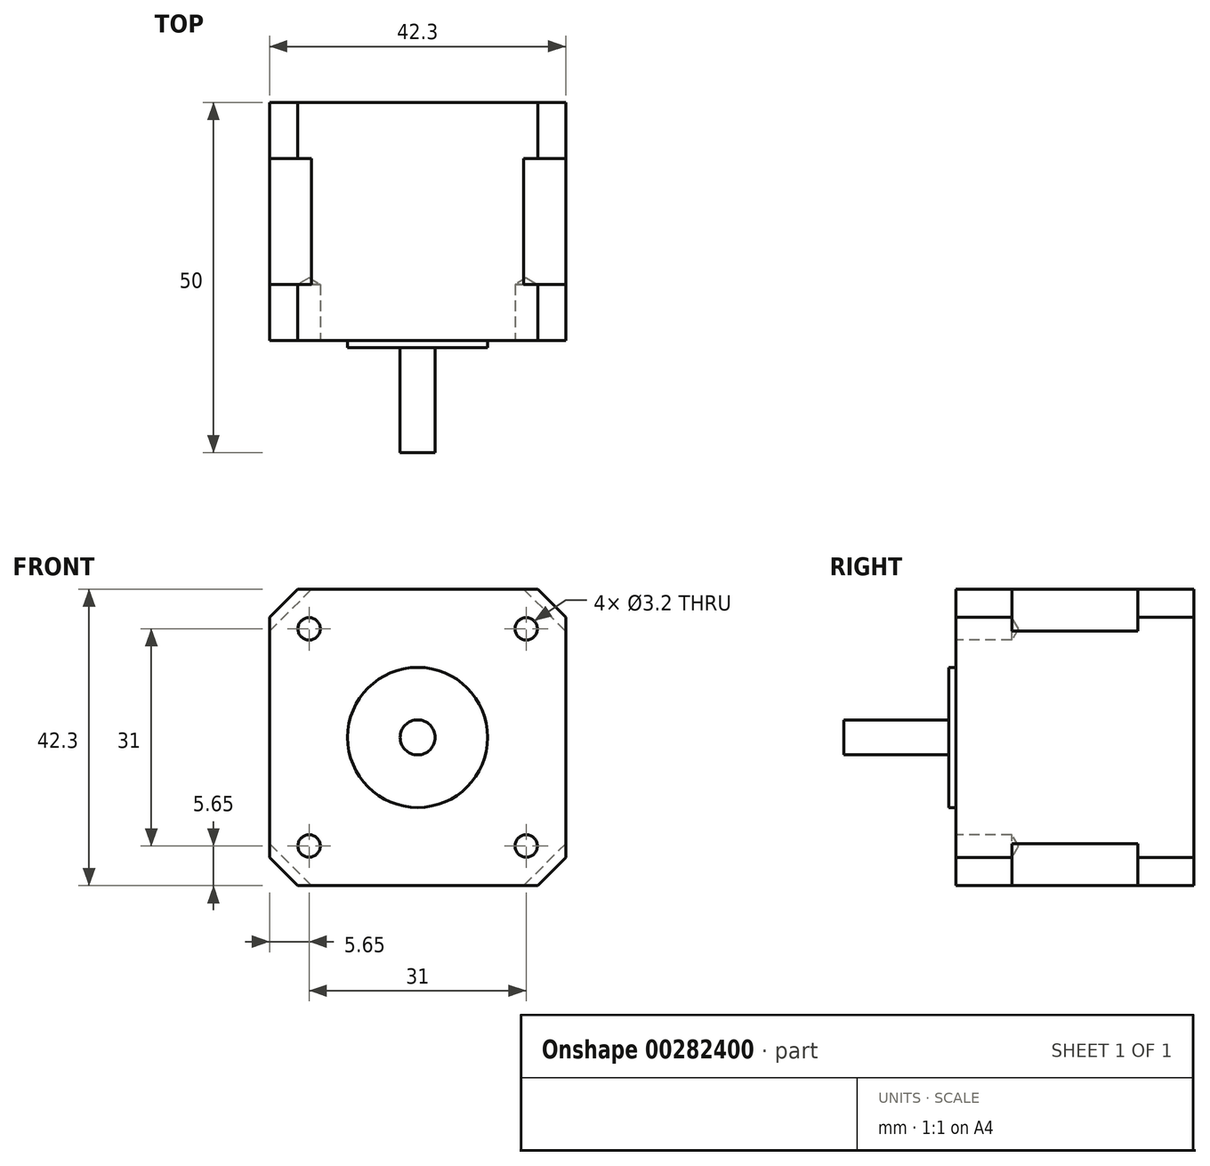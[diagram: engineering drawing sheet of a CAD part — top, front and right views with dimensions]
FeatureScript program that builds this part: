
annotation { "Feature Type Name" : "Feature", "Feature Type Description" : "" }
export const myFeature = defineFeature(function(context is Context, id is Id, definition is map)
    precondition{}
    {
        {
            var Q0;
            Q0=qCreatedBy(makeId("Front.planeOp"),FACE);
            var sketch = newSketch(context, id + "F0", { "sketchPlane" : qUnion([Q0])});
            skLineSegment(sketch, "E0.bottom", {"start": v(-17.15, -21.15) * mm, "end": v(17.15, -21.15) * mm});
            skLineSegment(sketch, "E0.top", {"start": v(-17.15, 21.15) * mm, "end": v(17.15, 21.15) * mm});
            skLineSegment(sketch, "E0.left", {"start": v(-21.15, -17.15) * mm, "end": v(-21.15, 17.15) * mm});
            skLineSegment(sketch, "E0.right", {"start": v(21.15, -17.15) * mm, "end": v(21.15, 17.15) * mm});
            skPoint(sketch, "E0.middle", {"position": v(0, 0) * mm});
            skLineSegment(sketch, "E1", {"start": v(17.15, 21.15) * mm, "end": v(21.15, 17.15) * mm});
            skLineSegment(sketch, "E2", {"start": v(-21.15, 17.15) * mm, "end": v(-17.15, 21.15) * mm});
            skLineSegment(sketch, "E3", {"start": v(-21.15, -17.15) * mm, "end": v(-17.15, -21.15) * mm});
            skLineSegment(sketch, "E4", {"start": v(17.15, -21.15) * mm, "end": v(21.15, -17.15) * mm});
            skPoint(sketch, "E5.orphan", {"position": v(-21.15, 21.15) * mm});
            skPoint(sketch, "E6.orphan", {"position": v(21.15, 21.15) * mm});
            skPoint(sketch, "E7.orphan", {"position": v(21.15, -21.15) * mm});
            skPoint(sketch, "E8.orphan", {"position": v(-21.15, -21.15) * mm});
            skSolve(sketch);
        }
        {
            var Q0;
            Q0=qSketchRegion(id+"F0",true);
            extrude(context, id + "F1", {"entities" : qUnion([Q0]), "depth" : 8 * mm});
        }
        {
            var Q0;
            Q0=makeQuery(id+"F1.opExtrude","CAP_FACE",FACE,{"disambiguationData":[OSD([sQuery(id+"F0.wireOp",EDGE,"E0.bottom"),sQuery(id+"F0.wireOp",EDGE,"E0.top"),sQuery(id+"F0.wireOp",EDGE,"E0.left"),sQuery(id+"F0.wireOp",EDGE,"E0.right"),sQuery(id+"F0.wireOp",EDGE,"E1"),sQuery(id+"F0.wireOp",EDGE,"E2"),sQuery(id+"F0.wireOp",EDGE,"E3"),sQuery(id+"F0.wireOp",EDGE,"E4")])],"isStart":false});
            var sketch = newSketch(context, id + "F2", { "sketchPlane" : qUnion([Q0])});
            skLineSegment(sketch, "E9", {"start": v(-21.15, -15.15) * mm, "end": v(-21.15, 15.15) * mm});
            skLineSegment(sketch, "E10", {"start": v(-21.15, 15.15) * mm, "end": v(-15.15, 21.15) * mm});
            skLineSegment(sketch, "E11", {"start": v(-15.15, 21.15) * mm, "end": v(15.15, 21.15) * mm});
            skLineSegment(sketch, "E12", {"start": v(15.15, 21.15) * mm, "end": v(21.15, 15.15) * mm});
            skLineSegment(sketch, "E13", {"start": v(21.15, 15.15) * mm, "end": v(21.15, -15.15) * mm});
            skLineSegment(sketch, "E14", {"start": v(21.15, -15.15) * mm, "end": v(15.15, -21.15) * mm});
            skLineSegment(sketch, "E15", {"start": v(15.15, -21.15) * mm, "end": v(-15.15, -21.15) * mm});
            skLineSegment(sketch, "E16", {"start": v(-15.15, -21.15) * mm, "end": v(-21.15, -15.15) * mm});
            skSolve(sketch);
        }
        {
            var Q0;
            Q0=qSketchRegion(id+"F2",true);
            extrude(context, id + "F3", {"entities" : qUnion([Q0]), "operationType" : NewBodyOperationType.ADD, "depth" : 18 * mm});
        }
        {
            var Q0;
            Q0=makeQuery(id+"F3.opExtrude","CAP_FACE",FACE,{"disambiguationData":[OSD([sQuery(id+"F2.wireOp",EDGE,"E9"),sQuery(id+"F2.wireOp",EDGE,"E10"),sQuery(id+"F2.wireOp",EDGE,"E11"),sQuery(id+"F2.wireOp",EDGE,"E12"),sQuery(id+"F2.wireOp",EDGE,"E13"),sQuery(id+"F2.wireOp",EDGE,"E14"),sQuery(id+"F2.wireOp",EDGE,"E15"),sQuery(id+"F2.wireOp",EDGE,"E16")])],"isStart":false});
            var sketch = newSketch(context, id + "F4", { "sketchPlane" : qUnion([Q0])});
            skLineSegment(sketch, "E17", {"start": v(-21.15, -17.15) * mm, "end": v(-21.15, 17.15) * mm});
            skLineSegment(sketch, "E18", {"start": v(-21.15, 17.15) * mm, "end": v(-17.15, 21.15) * mm});
            skLineSegment(sketch, "E19", {"start": v(-17.15, 21.15) * mm, "end": v(17.15, 21.15) * mm});
            skLineSegment(sketch, "E20", {"start": v(17.15, 21.15) * mm, "end": v(21.15, 17.15) * mm});
            skLineSegment(sketch, "E21", {"start": v(21.15, 17.15) * mm, "end": v(21.15, -17.15) * mm});
            skLineSegment(sketch, "E22", {"start": v(21.15, -17.15) * mm, "end": v(17.15, -21.15) * mm});
            skLineSegment(sketch, "E23", {"start": v(17.15, -21.15) * mm, "end": v(-17.15, -21.15) * mm});
            skLineSegment(sketch, "E24", {"start": v(-17.15, -21.15) * mm, "end": v(-21.15, -17.15) * mm});
            skSolve(sketch);
        }
        {
            var Q0;
            Q0=qSketchRegion(id+"F4",true);
            extrude(context, id + "F5", {"entities" : qUnion([Q0]), "operationType" : NewBodyOperationType.ADD, "depth" : 8 * mm});
        }
        {
            var Q0;
            Q0=makeQuery(id+"F5.opExtrude","CAP_FACE",FACE,{"disambiguationData":[OSD([sQuery(id+"F4.wireOp",EDGE,"E17"),sQuery(id+"F4.wireOp",EDGE,"E18"),sQuery(id+"F4.wireOp",EDGE,"E19"),sQuery(id+"F4.wireOp",EDGE,"E20"),sQuery(id+"F4.wireOp",EDGE,"E21"),sQuery(id+"F4.wireOp",EDGE,"E22"),sQuery(id+"F4.wireOp",EDGE,"E23"),sQuery(id+"F4.wireOp",EDGE,"E24")])],"isStart":false});
            var sketch = newSketch(context, id + "F6", { "sketchPlane" : qUnion([Q0])});
            skCircle(sketch, "E25", {"center": v(0, 0) * mm, "radius": 10 * mm});
            skSolve(sketch);
        }
        {
            var Q0;
            Q0=qSketchRegion(id+"F6",true);
            extrude(context, id + "F7", {"entities" : qUnion([Q0]), "operationType" : NewBodyOperationType.ADD, "depth" : 1 * mm});
        }
        {
            var Q0;
            Q0=makeQuery(id+"F5.opExtrude","CAP_FACE",FACE,{"disambiguationData":[OSD([sQuery(id+"F4.wireOp",EDGE,"E17"),sQuery(id+"F4.wireOp",EDGE,"E18"),sQuery(id+"F4.wireOp",EDGE,"E19"),sQuery(id+"F4.wireOp",EDGE,"E20"),sQuery(id+"F4.wireOp",EDGE,"E21"),sQuery(id+"F4.wireOp",EDGE,"E22"),sQuery(id+"F4.wireOp",EDGE,"E23"),sQuery(id+"F4.wireOp",EDGE,"E24")])],"isStart":false});
            var sketch = newSketch(context, id + "F8", { "sketchPlane" : qUnion([Q0])});
            skPoint(sketch, "E26", {"position": v(-15.5, 15.5) * mm});
            skPoint(sketch, "E27", {"position": v(15.5, 15.5) * mm});
            skPoint(sketch, "E28", {"position": v(15.5, -15.5) * mm});
            skPoint(sketch, "E29", {"position": v(-15.5, -15.5) * mm});
            skSolve(sketch);
        }
        {
            var Q0;
            Q0=sQuery(id+"F8.wireOp",VERTEX,"E26");
            var Q1;
            Q1=sQuery(id+"F8.wireOp",VERTEX,"E27");
            var Q2;
            Q2=sQuery(id+"F8.wireOp",VERTEX,"E28");
            var Q3;
            Q3=sQuery(id+"F8.wireOp",VERTEX,"E29");
            var Q4;
            Q4=makeQuery(id+"F1.opExtrude","SWEPT_BODY",BODY,{"disambiguationData":[OSD([sQuery(id+"F0.wireOp",EDGE,"E0.bottom"),sQuery(id+"F0.wireOp",EDGE,"E0.top"),sQuery(id+"F0.wireOp",EDGE,"E0.left"),sQuery(id+"F0.wireOp",EDGE,"E0.right"),sQuery(id+"F0.wireOp",EDGE,"E1"),sQuery(id+"F0.wireOp",EDGE,"E2"),sQuery(id+"F0.wireOp",EDGE,"E3"),sQuery(id+"F0.wireOp",EDGE,"E4")])]});
            hole(context, id + "F9", {"style" : HoleStyle.SIMPLE, "endStyle" : HoleEndStyle.BLIND, "standardTappedOrClearance" : lookupTablePath({ "standard" : "ISO", "engagement" : "75%", "pitch" : "0.75 mm", "size" : "M4", "type" : "Tapped" }), "standardBlindInLast" : lookupTablePath({ "standard" : "ISO", "engagement" : "75%", "pitch" : "0.75 mm", "size" : "M4", "type" : "Tapped" }), "holeDiameter" : 3.2 * mm, "holeDepth" : 8 * mm, "startFromSketch" : true, "locations" : qUnion([Q0, Q1, Q2, Q3]), "scope" : qUnion([Q4])});
        }
        {
            var Q0;
            Q0=makeQuery(id+"F7.opExtrude","CAP_FACE",FACE,{"disambiguationData":[OSD([sQuery(id+"F6.wireOp",EDGE,"E25")])],"isStart":false});
            var sketch = newSketch(context, id + "F10", { "sketchPlane" : qUnion([Q0])});
            skCircle(sketch, "E30", {"center": v(0, 0) * mm, "radius": 2.5 * mm});
            skSolve(sketch);
        }
        {
            var Q0;
            Q0=qSketchRegion(id+"F10",true);
            extrude(context, id + "F11", {"entities" : qUnion([Q0]), "operationType" : NewBodyOperationType.ADD, "depth" : 15 * mm});
        }
    });
